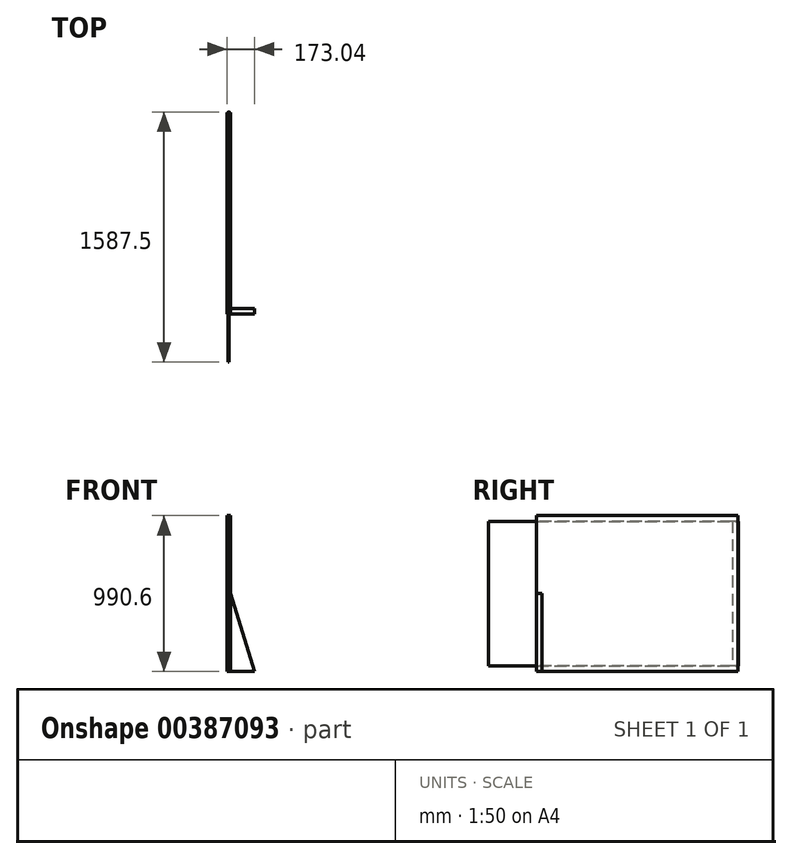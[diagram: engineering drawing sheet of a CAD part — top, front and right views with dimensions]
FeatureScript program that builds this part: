
annotation { "Feature Type Name" : "Feature", "Feature Type Description" : "" }
export const myFeature = defineFeature(function(context is Context, id is Id, definition is map)
    precondition{}
    {
        {
            var Q0;
            Q0=qCreatedBy(makeId("Right.planeOp"),FACE);
            var sketch = newSketch(context, id + "F0", { "sketchPlane" : qUnion([Q0])});
            skLineSegment(sketch, "E0.bottom", {"start": v(0, 0) * mm, "end": v(2501.9, 0) * mm, "construction": true});
            skLineSegment(sketch, "E0.top", {"start": v(0, 914.4) * mm, "end": v(2501.9, 914.4) * mm, "construction": true});
            skLineSegment(sketch, "E0.left", {"start": v(0, 0) * mm, "end": v(0, 914.4) * mm, "construction": true});
            skLineSegment(sketch, "E0.right", {"start": v(2501.9, 0) * mm, "end": v(2501.9, 914.4) * mm, "construction": true});
            skLineSegment(sketch, "E1", {"start": v(1219.2, 914.4) * mm, "end": v(1219.2, 0) * mm, "construction": true});
            skSolve(sketch);
        }
        {
            var Q0;
            Q0=qCreatedBy(makeId("Right.planeOp"),FACE);
            var sketch = newSketch(context, id + "F1", { "sketchPlane" : qUnion([Q0])});
            skLineSegment(sketch, "E2", {"start": v(1219.2, 0) * mm, "end": v(2499.8, 0) * mm});
            skLineSegment(sketch, "E3", {"start": v(2499.8, 0) * mm, "end": v(2499.8, 990.6) * mm});
            skLineSegment(sketch, "E4", {"start": v(2499.8, 990.6) * mm, "end": v(1219.2, 990.6) * mm});
            skLineSegment(sketch, "E5", {"start": v(1219.2, 990.6) * mm, "end": v(1219.2, 0) * mm});
            skSolve(sketch);
        }
        {
            var Q0;
            Q0 = qSketchRegion(id + "F1", true);
            extrude(context, id + "F2", {"entities" : qUnion([Q0]), "depth" : 6.35 * mm});
        }
        {
            var Q0;
            Q0=makeQuery(id+"F2.opExtrude","CAP_FACE",FACE,{"disambiguationData":[OSD([sQuery(id+"F1.wireOp",EDGE,"E2"),sQuery(id+"F1.wireOp",EDGE,"E3"),sQuery(id+"F1.wireOp",EDGE,"E4"),sQuery(id+"F1.wireOp",EDGE,"E5")])],"isStart":false});
            var sketch = newSketch(context, id + "F3", { "sketchPlane" : qUnion([Q0])});
            skLineSegment(sketch, "E6.bottom", {"start": v(1219.2, 990.6) * mm, "end": v(2499.8, 990.6) * mm});
            skLineSegment(sketch, "E6.top", {"start": v(1219.2, 954.09) * mm, "end": v(2499.8, 954.09) * mm});
            skLineSegment(sketch, "E6.left", {"start": v(1219.2, 990.6) * mm, "end": v(1219.2, 954.09) * mm});
            skLineSegment(sketch, "E6.right", {"start": v(2499.8, 990.6) * mm, "end": v(2499.8, 954.09) * mm});
            skLineSegment(sketch, "E7", {"start": v(1219.2, 495.3) * mm, "end": v(2499.8, 495.3) * mm, "construction": true});
            skLineSegment(sketch, "E8.MirrorCS", {"start": v(1219.2, 0) * mm, "end": v(1219.2, 36.51) * mm});
            skLineSegment(sketch, "E9.MirrorCS", {"start": v(2499.8, 0) * mm, "end": v(2499.8, 36.51) * mm});
            skLineSegment(sketch, "E10.MirrorCS", {"start": v(1219.2, 0) * mm, "end": v(2499.8, 0) * mm});
            skLineSegment(sketch, "E11.MirrorCS", {"start": v(1219.2, 36.51) * mm, "end": v(2499.8, 36.51) * mm});
            skSolve(sketch);
        }
        {
            var Q0;
            Q0 = qSketchRegion(id + "F3", true);
            extrude(context, id + "F4", {"entities" : qUnion([Q0]), "depth" : 7.94 * mm});
        }
        {
            var Q0;
            Q0=makeQuery(id+"F2.opExtrude","CAP_FACE",FACE,{"disambiguationData":[OSD([sQuery(id+"F1.wireOp",EDGE,"E2"),sQuery(id+"F1.wireOp",EDGE,"E3"),sQuery(id+"F1.wireOp",EDGE,"E4"),sQuery(id+"F1.wireOp",EDGE,"E5")])],"isStart":false});
            var sketch = newSketch(context, id + "F5", { "sketchPlane" : qUnion([Q0])});
            skLineSegment(sketch, "E12.bottom", {"start": v(2501.9, 954.09) * mm, "end": v(2463.8, 954.09) * mm});
            skLineSegment(sketch, "E12.top", {"start": v(2501.9, 36.51) * mm, "end": v(2463.8, 36.51) * mm});
            skLineSegment(sketch, "E12.left", {"start": v(2501.9, 954.09) * mm, "end": v(2501.9, 36.51) * mm});
            skLineSegment(sketch, "E12.right", {"start": v(2463.8, 954.09) * mm, "end": v(2463.8, 36.51) * mm});
            skSolve(sketch);
        }
        {
            var Q0;
            Q0 = qSketchRegion(id + "F5", true);
            var Q1;
            Q1=makeQuery(id+"F4.opExtrude","CAP_FACE",FACE,{"disambiguationData":[OSD([sQuery(id+"F3.wireOp",EDGE,"E6.bottom"),sQuery(id+"F3.wireOp",EDGE,"E6.top"),sQuery(id+"F3.wireOp",EDGE,"E6.left"),sQuery(id+"F3.wireOp",EDGE,"E6.right")])],"isStart":false});
            extrude(context, id + "F6", {"entities" : qUnion([Q0]), "endBound" : BoundingType.UP_TO_SURFACE, "endBoundEntityFace" : qUnion([Q1]), "depth" : 7.14 * mm});
        }
        {
            var Q0;
            Q0=makeQuery(id+"F2.opExtrude","CAP_FACE",FACE,{"disambiguationData":[OSD([sQuery(id+"F1.wireOp",EDGE,"E2"),sQuery(id+"F1.wireOp",EDGE,"E3"),sQuery(id+"F1.wireOp",EDGE,"E4"),sQuery(id+"F1.wireOp",EDGE,"E5")])],"isStart":false});
            var sketch = newSketch(context, id + "F7", { "sketchPlane" : qUnion([Q0])});
            skLineSegment(sketch, "E13.0", {"start": v(2463.8, 954.09) * mm, "end": v(2463.8, 36.51) * mm});
            skLineSegment(sketch, "E14", {"start": v(2463.8, 954.09) * mm, "end": v(914.4, 954.09) * mm});
            skLineSegment(sketch, "E15", {"start": v(2463.8, 36.51) * mm, "end": v(914.4, 36.51) * mm});
            skLineSegment(sketch, "E16", {"start": v(914.4, 36.51) * mm, "end": v(914.4, 954.09) * mm});
            skSolve(sketch);
        }
        {
            var Q0;
            Q0 = qSketchRegion(id + "F7", true);
            extrude(context, id + "F8", {"entities" : qUnion([Q0]), "depth" : 6.35 * mm});
        }
        {
            var Q0;
            Q0=makeQuery(id+"F4.opExtrude","CAP_FACE",FACE,{"disambiguationData":[OSD([sQuery(id+"F3.wireOp",EDGE,"E6.bottom"),sQuery(id+"F3.wireOp",EDGE,"E6.top"),sQuery(id+"F3.wireOp",EDGE,"E6.left"),sQuery(id+"F3.wireOp",EDGE,"E6.right")])],"isStart":false});
            var sketch = newSketch(context, id + "F9", { "sketchPlane" : qUnion([Q0])});
            skLineSegment(sketch, "E17.0.0", {"start": v(1219.2, 990.6) * mm, "end": v(2499.8, 990.6) * mm});
            skLineSegment(sketch, "E17.0.1", {"start": v(2499.8, 990.6) * mm, "end": v(2499.8, 0) * mm});
            skLineSegment(sketch, "E17.0.2", {"start": v(2499.8, 0) * mm, "end": v(1219.2, 0) * mm});
            skLineSegment(sketch, "E17.0.3", {"start": v(1219.2, 0) * mm, "end": v(1219.2, 990.6) * mm});
            skSolve(sketch);
        }
        {
            var Q0;
            Q0 = qSketchRegion(id + "F9", true);
            extrude(context, id + "F10", {"entities" : qUnion([Q0]), "depth" : 6.35 * mm});
        }
        {
            var Q0;
            Q0=makeQuery(id+"F10.opExtrude","SWEPT_FACE",FACE,{"disambiguationData":[OSD([sQuery(id+"F9.wireOp",EDGE,"E17.0.3")])]});
            var sketch = newSketch(context, id + "F11", { "sketchPlane" : qUnion([Q0])});
            skLineSegment(sketch, "E18", {"start": v(20.64, 0) * mm, "end": v(173.04, 0) * mm});
            skLineSegment(sketch, "E19", {"start": v(173.04, 0) * mm, "end": v(20.64, 495.3) * mm});
            skLineSegment(sketch, "E20", {"start": v(20.64, 495.3) * mm, "end": v(20.64, 0) * mm});
            skSolve(sketch);
        }
        {
            var Q0;
            Q0 = qSketchRegion(id + "F11", true);
            extrude(context, id + "F12", {"entities" : qUnion([Q0]), "oppositeDirection" : true, "depth" : 35.56 * mm});
        }
    });
